# Revit family: 306_a45e8535ca9c4dbf8485a23c1172b6
name_source: partatom
category: Pipe Accessories
units: mm (PartAtom-declared; Revit-internal decimal feet)

## family parameters
Always vertical = Yes
Cut with Voids When Loaded = No
Part Type = Valve - Breaks Into
Round Connector Dimension = Use Diameter
Shared = No
Work Plane-Based = No

## types (4) — shared parameters
B1 = 68 mm
B2 = 66 mm  [stored 0.216535 ft]
CAT0 = Yes
Description = 2-way motorized zone valve ZRS224, PN16 internal thread
H1 = 20 mm  [stored 0.0656168 ft]
L1 = 91 mm
L2 = 89 mm
L2D_Min = 3048 mm
Manufacturer = ESBE
QmdConnectorList = 301;D;302;D
R5 = 3 mm  [stored 0.00984252 ft]
R6 = 5 mm  [stored 0.0164042 ft]
R7 = 4 mm  [stored 0.0131234 ft]
URL = http://www.esbe.eu
X2 = 2 mm  [stored 0.00656168 ft]
magiPartTypeId = 306
magiProductFamilyId = a45e8535ca9c4dbf8485a23c1172b6

## per-type parameters (varying)
| type | C | D | DT2 | L2D | L5 | LT2 | LT4 | R1 | R2 | R3 | R4 | W2D | X1 | X1__ve | X3 | Z3 | Z4 | Z5 | Z6 | Z7 | magiProductCode | magiProductId |
| ZRS224 230VAC 2-P  20-4.6 G3/4 | 21 mm  [stored 0.0688976 ft] | 20 mm | 10 mm  [stored 0.0328084 ft] | 89 mm | 14 mm  [stored 0.0459318 ft] | 45 mm | 22 mm | 9 mm  [stored 0.0295276 ft] | 20 mm  [stored 0.0656168 ft] | 18 mm  [stored 0.0590551 ft] | 15 mm  [stored 0.0492126 ft] | 20 mm  [stored 0.0656168 ft] | 16 mm | -16 mm | 54 mm | 32 mm  [stored 0.104987 ft] | 2 mm  [stored 0.00656168 ft] | 4 mm  [stored 0.0131234 ft] | 11 mm  [stored 0.0360892 ft] | 20 mm  [stored 0.0656168 ft] | ZRS224 230VAC 2-P  20-4.6 G3/4" | 9aadf8143a5a45f79380943899d13c |
| ZRS224 230VAC 2-P 32-10 G11/4 | 30 mm  [stored 0.0984252 ft] | 32 mm | 16 mm | 105 mm | 17 mm  [stored 0.0557743 ft] | 53 mm | 26 mm | 14 mm  [stored 0.0459318 ft] | 24 mm  [stored 0.0787402 ft] | 21 mm  [stored 0.0688976 ft] | 18 mm  [stored 0.0590551 ft] | 32 mm  [stored 0.104987 ft] | 18 mm  [stored 0.0590551 ft] | -18 mm | 64 mm | 45 mm | 3 mm  [stored 0.00984252 ft] | 6 mm  [stored 0.019685 ft] | 9 mm  [stored 0.0295276 ft] | 21 mm  [stored 0.0688976 ft] | ZRS224 230VAC 2-P 32-10 G11/4" | 7e5545d6a7b34e8980898ec20a215f |
| ZRS224 230VAC 2-P 25-5.7 G1 | 23 mm | 25 mm | 13 mm | 93 mm | 15 mm  [stored 0.0492126 ft] | 47 mm | 23 mm | 11 mm  [stored 0.0360892 ft] | 21 mm  [stored 0.0688976 ft] | 19 mm | 16 mm | 25 mm  [stored 0.082021 ft] | 16 mm | -16 mm | 56 mm  [stored 0.183727 ft] | 35 mm | 2 mm  [stored 0.00656168 ft] | 5 mm  [stored 0.0164042 ft] | 9 mm  [stored 0.0295276 ft] | 18 mm  [stored 0.0590551 ft] | ZRS224 230VAC 2-P 25-5.7 G1" | ee28b963d5c84c2fbf338c36eb73a7 |
| ZRS224 230VAC 2-P 15-3.2 G1/2 | 21 mm  [stored 0.0688976 ft] | 15 mm | 8 mm  [stored 0.0262467 ft] | 80 mm | 12 mm  [stored 0.0393701 ft] | 40 mm | 20 mm  [stored 0.0656168 ft] | 7 mm  [stored 0.0229659 ft] | 18 mm  [stored 0.0590551 ft] | 16 mm | 13 mm | 15 mm  [stored 0.0492126 ft] | 14 mm  [stored 0.0459318 ft] | -14 mm | 48 mm  [stored 0.15748 ft] | 32 mm  [stored 0.104987 ft] | 2 mm  [stored 0.00656168 ft] | 4 mm  [stored 0.0131234 ft] | 11 mm  [stored 0.0360892 ft] | 23 mm | ZRS224 230VAC 2-P 15-3.2 G1/2" | b598ad7dcc514788b82497cada5d7b |

note: [stored X ft] marks values corroborated as IEEE doubles in the binary element streams (Revit-internal decimal feet)

## geometry (parser evidence)
native form markers: Sweep x3
no freeform markers — native parametric forms only
